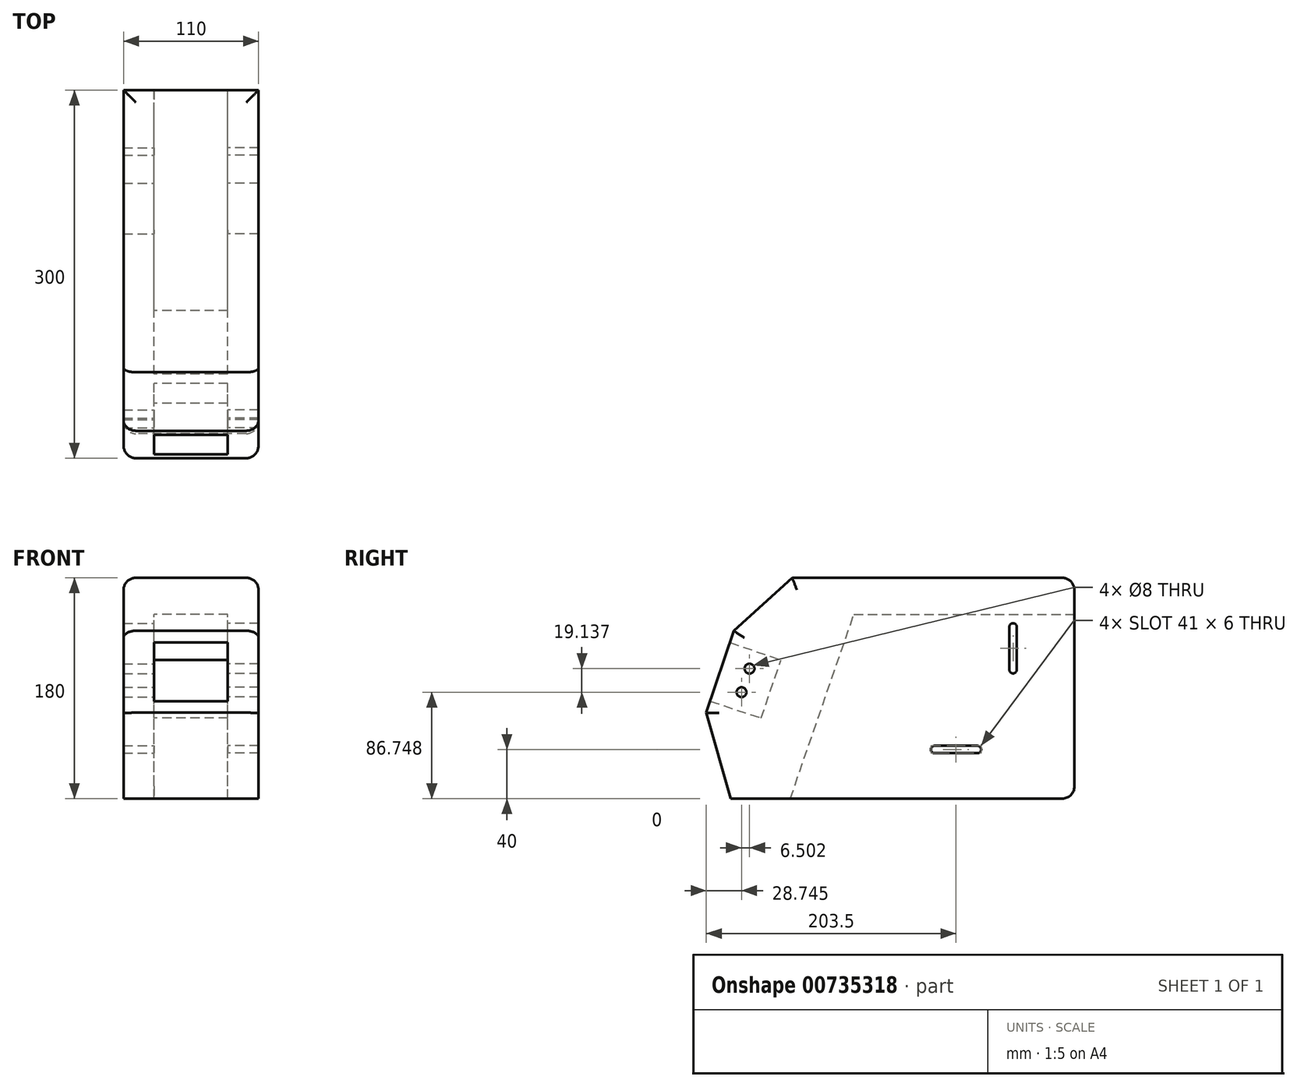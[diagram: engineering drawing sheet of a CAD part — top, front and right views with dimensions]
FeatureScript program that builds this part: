
annotation { "Feature Type Name" : "Feature", "Feature Type Description" : "" }
export const myFeature = defineFeature(function(context is Context, id is Id, definition is map)
    precondition{}
    {
        {
            var Q0;
            Q0=qCreatedBy(makeId("Right.planeOp"),FACE);
            var sketch = newSketch(context, id + "F0", { "sketchPlane" : qUnion([Q0])});
            skLineSegment(sketch, "E0.bottom", {"start": v(150, -90) * mm, "end": v(-150, -90) * mm, "construction": true});
            skLineSegment(sketch, "E0.top", {"start": v(150, 90) * mm, "end": v(-150, 90) * mm, "construction": true});
            skLineSegment(sketch, "E0.left", {"start": v(150, -90) * mm, "end": v(150, 90) * mm, "construction": true});
            skLineSegment(sketch, "E0.right", {"start": v(-150, -90) * mm, "end": v(-150, 90) * mm, "construction": true});
            skPoint(sketch, "E0.middle", {"position": v(0, 0) * mm});
            skLineSegment(sketch, "E1", {"start": v(-150, -20) * mm, "end": v(-113.22, 90) * mm, "construction": true});
            skLineSegment(sketch, "E2", {"start": v(-150, -20) * mm, "end": v(-92.1, -20) * mm, "construction": true});
            skLineSegment(sketch, "E3", {"start": v(-105.33, -24.4) * mm, "end": v(-89.02, 22.87) * mm});
            skLineSegment(sketch, "E4", {"start": v(-127.67, 46.79) * mm, "end": v(-130.84, 37.3) * mm});
            skLineSegment(sketch, "E5", {"start": v(-130.84, 37.3) * mm, "end": v(-89.02, 22.87) * mm});
            skLineSegment(sketch, "E6", {"start": v(-150, -20) * mm, "end": v(-146.83, -10.52) * mm});
            skLineSegment(sketch, "E7", {"start": v(-146.83, -10.52) * mm, "end": v(-105.33, -24.4) * mm});
            skLineSegment(sketch, "E8", {"start": v(-109.93, 30.09) * mm, "end": v(-126.08, -17.45) * mm, "construction": true});
            skCircle(sketch, "E9", {"center": v(-114.75, 15.89) * mm, "radius": 4 * mm, "construction": true});
            skCircle(sketch, "E10", {"center": v(-121.25, -3.25) * mm, "radius": 4 * mm, "construction": true});
            skLineSegment(sketch, "E11", {"start": v(-150, -20) * mm, "end": v(-130, -90) * mm});
            skLineSegment(sketch, "E12", {"start": v(-130, -90) * mm, "end": v(-81.49, -90) * mm});
            skLineSegment(sketch, "E13", {"start": v(-81.49, -90) * mm, "end": v(-29.72, 60) * mm});
            skLineSegment(sketch, "E14", {"start": v(-29.72, 60) * mm, "end": v(150, 60) * mm});
            skLineSegment(sketch, "E15", {"start": v(150, 60) * mm, "end": v(150, 90) * mm});
            skLineSegment(sketch, "E16", {"start": v(-127.67, 46.79) * mm, "end": v(-80, 90) * mm});
            skLineSegment(sketch, "E17", {"start": v(-80, 90) * mm, "end": v(150, 90) * mm});
            skLineSegment(sketch, "E18", {"start": v(-29.72, 60) * mm, "end": v(-19.36, 90) * mm});
            skLineSegment(sketch, "E19", {"start": v(-19.36, 90) * mm, "end": v(-24.54, 75) * mm});
            skSolve(sketch);
        }
        {
            var Q0;
            {var subQ4=sQuery(id+"F0.wireOp",EDGE,"E14");Q0=qUnion([makeQuery(id+"F0.imprint","IMPRINT",FACE,{"disambiguationData":[TD([[makeQuery(id+"F0.imprint","IMPRINT",EDGE,{"derivedFrom":sQuery(id+"F0.wireOp",EDGE,"E3")}),-1.0]])]}),makeQuery(id+"F0.imprint","IMPRINT",FACE,{"disambiguationData":[TD([[makeQuery(id+"F0.imprint","IMPRINT",EDGE,{"derivedFrom":subQ4}),1.0]])]})]);}
            extrude(context, id + "F1", {"entities" : qUnion([Q0]), "endBound" : BoundingType.SYMMETRIC, "depth" : 60 * mm, "offsetDistance" : 25 * mm});
        }
        {
            var Q0;
            Q0=makeQuery(id+"F1.opExtrude","CAP_FACE",FACE,{"disambiguationData":[OSD([sQuery(id+"F0.wireOp",EDGE,"E3"),sQuery(id+"F0.wireOp",EDGE,"E4"),sQuery(id+"F0.wireOp",EDGE,"E5"),sQuery(id+"F0.wireOp",EDGE,"E6"),sQuery(id+"F0.wireOp",EDGE,"E7"),sQuery(id+"F0.wireOp",EDGE,"E11"),sQuery(id+"F0.wireOp",EDGE,"E12"),sQuery(id+"F0.wireOp",EDGE,"E13"),sQuery(id+"F0.wireOp",EDGE,"E14"),sQuery(id+"F0.wireOp",EDGE,"E15"),sQuery(id+"F0.wireOp",EDGE,"E16"),sQuery(id+"F0.wireOp",EDGE,"E17")])],"isStart":false});
            var sketch = newSketch(context, id + "F2", { "sketchPlane" : qUnion([Q0])});
            skLineSegment(sketch, "E20", {"start": v(-127.67, 46.79) * mm, "end": v(-80, 90) * mm});
            skLineSegment(sketch, "E21", {"start": v(-80, 90) * mm, "end": v(150, 90) * mm});
            skLineSegment(sketch, "E22", {"start": v(150, -90) * mm, "end": v(-130, -90) * mm});
            skLineSegment(sketch, "E23", {"start": v(-130, -90) * mm, "end": v(-150, -20) * mm});
            skLineSegment(sketch, "E24", {"start": v(-150, -20) * mm, "end": v(-127.67, 46.79) * mm});
            skLineSegment(sketch, "E25", {"start": v(36, -50) * mm, "end": v(71, -50) * mm, "construction": true});
            skLineSegment(sketch, "E26", {"start": v(71, -50) * mm, "end": v(100, -50) * mm, "construction": true});
            skLineSegment(sketch, "E27", {"start": v(100, -50) * mm, "end": v(100, 15) * mm, "construction": true});
            skLineSegment(sketch, "E28", {"start": v(100, 15) * mm, "end": v(100, 50) * mm, "construction": true});
            skLineSegment(sketch, "E29", {"start": v(150, 90) * mm, "end": v(150, -90) * mm});
            skArc(sketch, "E30.0.startCap", {"start": v(103, 15) * mm, "mid": v(100, 12) * mm, "end": v(97, 15) * mm});
            skArc(sketch, "E30.0.endCap", {"start": v(97, 50) * mm, "mid": v(100, 53) * mm, "end": v(103, 50) * mm});
            skLineSegment(sketch, "E30.0.left", {"start": v(97, 15) * mm, "end": v(97, 50) * mm});
            skLineSegment(sketch, "E30.0.right", {"start": v(103, 15) * mm, "end": v(103, 50) * mm});
            skArc(sketch, "E31.0.startCap", {"start": v(36, -53) * mm, "mid": v(33, -50) * mm, "end": v(36, -47) * mm});
            skArc(sketch, "E31.0.endCap", {"start": v(71, -47) * mm, "mid": v(74, -50) * mm, "end": v(71, -53) * mm});
            skLineSegment(sketch, "E31.0.left", {"start": v(36, -47) * mm, "end": v(71, -47) * mm});
            skLineSegment(sketch, "E31.0.right", {"start": v(36, -53) * mm, "end": v(71, -53) * mm});
            skCircle(sketch, "E32.0", {"center": v(-114.75, 15.89) * mm, "radius": 4 * mm});
            skCircle(sketch, "E32.1", {"center": v(-121.25, -3.25) * mm, "radius": 4 * mm});
            skSolve(sketch);
        }
        {
            var Q0;
            Q0=qSketchRegion(id+"F2",true);
            extrude(context, id + "F3", {"entities" : qUnion([Q0]), "operationType" : NewBodyOperationType.ADD, "depth" : 25 * mm, "offsetDistance" : 25 * mm});
        }
        {
            var Q0;
            Q0=makeQuery(id+"F1.opExtrude","CAP_FACE",FACE,{"disambiguationData":[OSD([sQuery(id+"F0.wireOp",EDGE,"E3"),sQuery(id+"F0.wireOp",EDGE,"E4"),sQuery(id+"F0.wireOp",EDGE,"E5"),sQuery(id+"F0.wireOp",EDGE,"E6"),sQuery(id+"F0.wireOp",EDGE,"E7"),sQuery(id+"F0.wireOp",EDGE,"E11"),sQuery(id+"F0.wireOp",EDGE,"E12"),sQuery(id+"F0.wireOp",EDGE,"E13"),sQuery(id+"F0.wireOp",EDGE,"E14"),sQuery(id+"F0.wireOp",EDGE,"E15"),sQuery(id+"F0.wireOp",EDGE,"E16"),sQuery(id+"F0.wireOp",EDGE,"E17")])],"isStart":true});
            var sketch = newSketch(context, id + "F4", { "sketchPlane" : qUnion([Q0])});
            skLineSegment(sketch, "E33.0.0", {"start": v(127.67, 46.79) * mm, "end": v(150, -20) * mm});
            skLineSegment(sketch, "E33.0.1", {"start": v(150, -20) * mm, "end": v(130, -90) * mm});
            skLineSegment(sketch, "E33.0.2", {"start": v(130, -90) * mm, "end": v(-150, -90) * mm});
            skLineSegment(sketch, "E33.0.3", {"start": v(-150, -90) * mm, "end": v(-150, 90) * mm});
            skLineSegment(sketch, "E33.0.4", {"start": v(-150, 90) * mm, "end": v(80, 90) * mm});
            skLineSegment(sketch, "E33.0.5", {"start": v(80, 90) * mm, "end": v(127.67, 46.79) * mm});
            skLineSegment(sketch, "E34.0", {"start": v(-103, 15) * mm, "end": v(-103, 50) * mm});
            skArc(sketch, "E34.1", {"start": v(-97, 50) * mm, "mid": v(-100, 53) * mm, "end": v(-103, 50) * mm});
            skLineSegment(sketch, "E34.2", {"start": v(-97, 15) * mm, "end": v(-97, 50) * mm});
            skArc(sketch, "E34.3", {"start": v(-103, 15) * mm, "mid": v(-100, 12) * mm, "end": v(-97, 15) * mm});
            skLineSegment(sketch, "E34.4", {"start": v(-36, -47) * mm, "end": v(-71, -47) * mm});
            skLineSegment(sketch, "E34.5", {"start": v(-36, -53) * mm, "end": v(-71, -53) * mm});
            skArc(sketch, "E34.6", {"start": v(-71, -47) * mm, "mid": v(-74, -50) * mm, "end": v(-71, -53) * mm});
            skArc(sketch, "E34.7", {"start": v(-36, -53) * mm, "mid": v(-33, -50) * mm, "end": v(-36, -47) * mm});
            skSolve(sketch);
        }
        {
            var Q0;
            Q0=makeQuery(id+"F4.imprint","IMPRINT",FACE,{"disambiguationData":[TD([[makeQuery(id+"F4.imprint","IMPRINT",EDGE,{"derivedFrom":sQuery(id+"F4.wireOp",EDGE,"E34.0")}),1.0]])]});
            var Q1;
            {var subQ7=sQuery(id+"F4.wireOp",EDGE,"E33.0.1");Q1=makeQuery(id+"F4.imprint","IMPRINT",FACE,{"disambiguationData":[TD([[makeQuery(id+"F4.imprint","IMPRINT",EDGE,{"derivedFrom":subQ7}),-1.0]])]});}
            var Q2;
            Q2=makeQuery(id+"F4.imprint","IMPRINT",FACE,{"disambiguationData":[TD([[makeQuery(id+"F4.imprint","IMPRINT",EDGE,{"derivedFrom":makeQuery(id+"F1.opExtrude","CAP_EDGE",EDGE,{"disambiguationData":[OSD([sQuery(id+"F0.wireOp",EDGE,"E3")])],"isStart":true})}),-1.0]])]});
            extrude(context, id + "F5", {"entities" : qUnion([Q0, Q1, Q2]), "operationType" : NewBodyOperationType.ADD, "depth" : 25 * mm, "offsetDistance" : 25 * mm});
        }
        {
            var Q0;
            Q0=makeQuery(id+"F3.opExtrude","CAP_EDGE",EDGE,{"disambiguationData":[OSD([sQuery(id+"F2.wireOp",EDGE,"E21")])],"isStart":false});
            var Q1;
            Q1=makeQuery(id+"F3.opExtrude","CAP_EDGE",EDGE,{"disambiguationData":[OSD([sQuery(id+"F2.wireOp",EDGE,"E20")])],"isStart":false});
            var Q2;
            Q2=makeQuery(id+"F3.opExtrude","CAP_EDGE",EDGE,{"disambiguationData":[OSD([sQuery(id+"F2.wireOp",EDGE,"E23")])],"isStart":false});
            var Q3;
            Q3=makeQuery(id+"F5.opExtrude","CAP_EDGE",EDGE,{"disambiguationData":[OSD([sQuery(id+"F4.wireOp",EDGE,"E33.0.1")])],"isStart":false});
            var Q4;
            Q4=makeQuery(id+"F5.opExtrude","CAP_EDGE",EDGE,{"disambiguationData":[OSD([sQuery(id+"F4.wireOp",EDGE,"E33.0.5")])],"isStart":false});
            var Q5;
            Q5=makeQuery(id+"F5.opExtrude","CAP_EDGE",EDGE,{"disambiguationData":[OSD([sQuery(id+"F4.wireOp",EDGE,"E33.0.4")])],"isStart":false});
            var Q6;
            Q6=makeQuery(id+"F5.boolean.opBoolean","MERGE",EDGE,{"derivedFrom":[makeQuery(id+"F3.boolean.opBoolean","MERGE",EDGE,{"derivedFrom":[makeQuery(id+"F1.opExtrude","SWEPT_EDGE",EDGE,{"disambiguationData":[OSD([sQuery(id+"F0.wireOp",EDGE,"E15"),sQuery(id+"F0.wireOp",EDGE,"E17")])]}),makeQuery(id+"F3.opExtrude","SWEPT_EDGE",EDGE,{"disambiguationData":[OSD([sQuery(id+"F2.wireOp",EDGE,"E21"),sQuery(id+"F2.wireOp",EDGE,"E29")])]})]}),makeQuery(id+"F5.opExtrude","SWEPT_EDGE",EDGE,{"disambiguationData":[OSD([sQuery(id+"F4.wireOp",EDGE,"E33.0.3"),sQuery(id+"F4.wireOp",EDGE,"E33.0.4")])]})]});
            var Q7;
            Q7=makeQuery(id+"F5.opExtrude","SWEPT_EDGE",EDGE,{"disambiguationData":[OSD([sQuery(id+"F4.wireOp",EDGE,"E33.0.2"),sQuery(id+"F4.wireOp",EDGE,"E33.0.3")])]});
            var Q8;
            Q8=makeQuery(id+"F3.opExtrude","SWEPT_EDGE",EDGE,{"disambiguationData":[OSD([sQuery(id+"F2.wireOp",EDGE,"E22"),sQuery(id+"F2.wireOp",EDGE,"E29")])]});
            var Q9;
            Q9=makeQuery(id+"F5.opExtrude","CAP_EDGE",EDGE,{"disambiguationData":[OSD([sQuery(id+"F4.wireOp",EDGE,"E33.0.0")])],"isStart":false});
            var Q10;
            Q10=makeQuery(id+"F3.opExtrude","CAP_EDGE",EDGE,{"disambiguationData":[OSD([sQuery(id+"F2.wireOp",EDGE,"E24")])],"isStart":false});
            fillet(context, id + "F6", {"entities" : qUnion([Q0, Q1, Q2, Q3, Q4, Q5, Q6, Q7, Q8, Q9, Q10]), "radius" : 10 * mm, "tangentPropagation" : true, "allowEdgeOverflow" : false});
        }
        {
            var Q0;
            Q0=sQuery(id+"F2.wireOp",VERTEX,"E32.0.center");
            var Q1;
            Q1=sQuery(id+"F2.wireOp",VERTEX,"E32.1.center");
            var Q2;
            Q2=makeQuery(id+"F1.opExtrude","SWEPT_BODY",BODY,{"disambiguationData":[OSD([sQuery(id+"F0.wireOp",EDGE,"E3"),sQuery(id+"F0.wireOp",EDGE,"E4"),sQuery(id+"F0.wireOp",EDGE,"E5"),sQuery(id+"F0.wireOp",EDGE,"E6"),sQuery(id+"F0.wireOp",EDGE,"E7"),sQuery(id+"F0.wireOp",EDGE,"E11"),sQuery(id+"F0.wireOp",EDGE,"E12"),sQuery(id+"F0.wireOp",EDGE,"E13"),sQuery(id+"F0.wireOp",EDGE,"E14"),sQuery(id+"F0.wireOp",EDGE,"E15"),sQuery(id+"F0.wireOp",EDGE,"E16"),sQuery(id+"F0.wireOp",EDGE,"E17")])]});
            hole(context, id + "F7", {"style" : HoleStyle.SIMPLE, "endStyle" : HoleEndStyle.THROUGH, "holeDiameter" : 8 * mm, "majorDiameter" : 5 * mm, "isTappedThrough" : true, "tappedDepth" : 12 * mm, "tapClearance" : 3, "locations" : qUnion([Q0, Q1]), "scope" : qUnion([Q2])});
        }
    });
